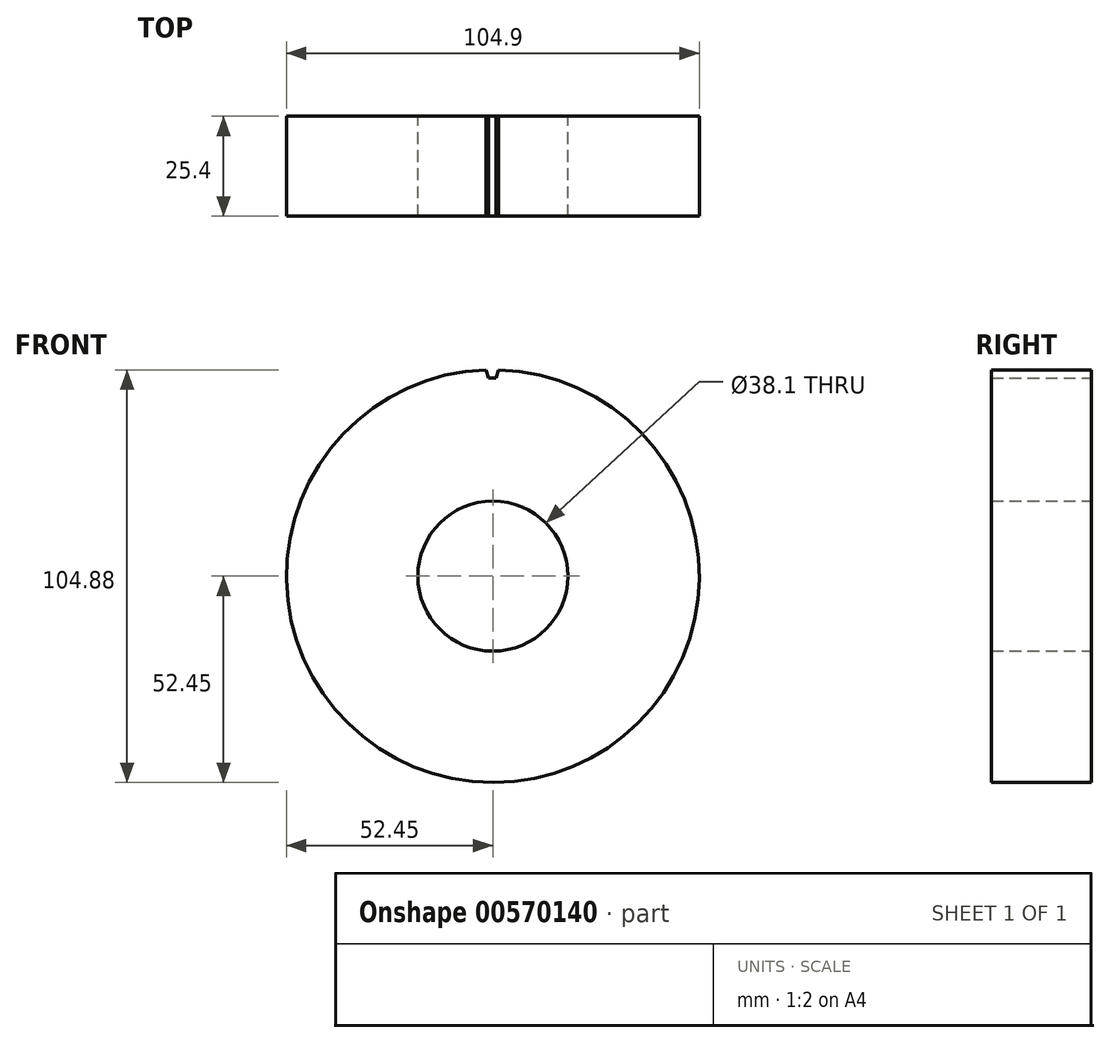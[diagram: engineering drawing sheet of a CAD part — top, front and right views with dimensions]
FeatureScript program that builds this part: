
annotation { "Feature Type Name" : "Feature", "Feature Type Description" : "" }
export const myFeature = defineFeature(function(context is Context, id is Id, definition is map)
    precondition{}
    {
        {
            var Q0;
            Q0=qCreatedBy(makeId("Front.planeOp"),FACE);
            var sketch = newSketch(context, id + "F0", { "sketchPlane" : qUnion([Q0])});
            skCircle(sketch, "E0", {"center": v(0, 0) * mm, "radius": 52.45 * mm});
            skCircle(sketch, "E1", {"center": v(0, 0) * mm, "radius": 19.05 * mm});
            skSolve(sketch);
        }
        {
            var Q0;
            Q0=makeQuery(id+"F0.imprint","IMPRINT",FACE,{"disambiguationData":[TD([[makeQuery(id+"F0.imprint","IMPRINT",EDGE,{"derivedFrom":sQuery(id+"F0.wireOp",EDGE,"E0")}),1.0]])]});
            extrude(context, id + "F1", {"entities" : qUnion([Q0]), "depth" : 25.4 * mm, "offsetDistance" : 25.4 * mm});
        }
        {
            var Q0;
            Q0=makeQuery(id+"F1.opExtrude","CAP_FACE",FACE,{"disambiguationData":[OSD([sQuery(id+"F0.wireOp",EDGE,"E0")])],"isStart":true});
            var sketch = newSketch(context, id + "F2", { "sketchPlane" : qUnion([Q0])});
            skLineSegment(sketch, "E2", {"start": v(-1.44, 52.43) * mm, "end": v(-0.83, 50.36) * mm});
            skLineSegment(sketch, "E3", {"start": v(-0.83, 50.36) * mm, "end": v(1.08, 50.36) * mm});
            skLineSegment(sketch, "E4", {"start": v(1.08, 50.36) * mm, "end": v(1.7, 52.42) * mm});
            skArc(sketch, "E5", {"start": v(1.7, 52.42) * mm, "mid": v(0.14, 52.45) * mm, "end": v(-1.44, 52.43) * mm});
            skSolve(sketch);
        }
        {
            var Q0;
            {var subQ0=sQuery(id+"F2.wireOp",EDGE,"E2");Q0=makeQuery(id+"F2.imprint","IMPRINT",FACE,{"disambiguationData":[TD([[makeQuery(id+"F2.imprint","IMPRINT",EDGE,{"derivedFrom":subQ0}),1.0]])]});}
            var Q1;
            Q1=makeQuery(id+"F32q0UH0prBzdGw_1.1.F2.imprint","IMPRINT",FACE,{"disambiguationData":[TD([[makeQuery(id+"F32q0UH0prBzdGw_1.1.F2.imprint","IMPRINT",EDGE,{"derivedFrom":sQuery(id+"F32q0UH0prBzdGw_1.1.F2.wireOp",EDGE,"E2")}),1.0]])]});
            var Q2;
            Q2=makeQuery(id+"F32q0UH0prBzdGw_1.2.F2.imprint","IMPRINT",FACE,{"disambiguationData":[TD([[makeQuery(id+"F32q0UH0prBzdGw_1.2.F2.imprint","IMPRINT",EDGE,{"derivedFrom":sQuery(id+"F32q0UH0prBzdGw_1.2.F2.wireOp",EDGE,"E2")}),1.0]])]});
            var Q3;
            Q3=makeQuery(id+"F32q0UH0prBzdGw_1.3.F2.imprint","IMPRINT",FACE,{"disambiguationData":[TD([[makeQuery(id+"F32q0UH0prBzdGw_1.3.F2.imprint","IMPRINT",EDGE,{"derivedFrom":sQuery(id+"F32q0UH0prBzdGw_1.3.F2.wireOp",EDGE,"E2")}),1.0]])]});
            var Q4;
            Q4=makeQuery(id+"F32q0UH0prBzdGw_1.4.F2.imprint","IMPRINT",FACE,{"disambiguationData":[TD([[makeQuery(id+"F32q0UH0prBzdGw_1.4.F2.imprint","IMPRINT",EDGE,{"derivedFrom":sQuery(id+"F32q0UH0prBzdGw_1.4.F2.wireOp",EDGE,"E2")}),1.0]])]});
            var Q5;
            Q5=makeQuery(id+"F32q0UH0prBzdGw_1.5.F2.imprint","IMPRINT",FACE,{"disambiguationData":[TD([[makeQuery(id+"F32q0UH0prBzdGw_1.5.F2.imprint","IMPRINT",EDGE,{"derivedFrom":sQuery(id+"F32q0UH0prBzdGw_1.5.F2.wireOp",EDGE,"E2")}),1.0]])]});
            var Q6;
            Q6=makeQuery(id+"F32q0UH0prBzdGw_1.59.F2.imprint","IMPRINT",FACE,{"disambiguationData":[TD([[makeQuery(id+"F32q0UH0prBzdGw_1.59.F2.imprint","IMPRINT",EDGE,{"derivedFrom":sQuery(id+"F32q0UH0prBzdGw_1.59.F2.wireOp",EDGE,"E2")}),1.0]])]});
            var Q7;
            Q7=makeQuery(id+"F32q0UH0prBzdGw_1.58.F2.imprint","IMPRINT",FACE,{"disambiguationData":[TD([[makeQuery(id+"F32q0UH0prBzdGw_1.58.F2.imprint","IMPRINT",EDGE,{"derivedFrom":sQuery(id+"F32q0UH0prBzdGw_1.58.F2.wireOp",EDGE,"E2")}),1.0]])]});
            var Q8;
            Q8=makeQuery(id+"F32q0UH0prBzdGw_1.6.F2.imprint","IMPRINT",FACE,{"disambiguationData":[TD([[makeQuery(id+"F32q0UH0prBzdGw_1.6.F2.imprint","IMPRINT",EDGE,{"derivedFrom":sQuery(id+"F32q0UH0prBzdGw_1.6.F2.wireOp",EDGE,"E2")}),1.0]])]});
            var Q9;
            Q9=makeQuery(id+"F32q0UH0prBzdGw_1.7.F2.imprint","IMPRINT",FACE,{"disambiguationData":[TD([[makeQuery(id+"F32q0UH0prBzdGw_1.7.F2.imprint","IMPRINT",EDGE,{"derivedFrom":sQuery(id+"F32q0UH0prBzdGw_1.7.F2.wireOp",EDGE,"E2")}),1.0]])]});
            var Q10;
            Q10=makeQuery(id+"F32q0UH0prBzdGw_1.8.F2.imprint","IMPRINT",FACE,{"disambiguationData":[TD([[makeQuery(id+"F32q0UH0prBzdGw_1.8.F2.imprint","IMPRINT",EDGE,{"derivedFrom":sQuery(id+"F32q0UH0prBzdGw_1.8.F2.wireOp",EDGE,"E2")}),1.0]])]});
            var Q11;
            Q11=makeQuery(id+"F32q0UH0prBzdGw_1.9.F2.imprint","IMPRINT",FACE,{"disambiguationData":[TD([[makeQuery(id+"F32q0UH0prBzdGw_1.9.F2.imprint","IMPRINT",EDGE,{"derivedFrom":sQuery(id+"F32q0UH0prBzdGw_1.9.F2.wireOp",EDGE,"E2")}),1.0]])]});
            var Q12;
            Q12=makeQuery(id+"F32q0UH0prBzdGw_1.10.F2.imprint","IMPRINT",FACE,{"disambiguationData":[TD([[makeQuery(id+"F32q0UH0prBzdGw_1.10.F2.imprint","IMPRINT",EDGE,{"derivedFrom":sQuery(id+"F32q0UH0prBzdGw_1.10.F2.wireOp",EDGE,"E2")}),1.0]])]});
            var Q13;
            Q13=makeQuery(id+"F32q0UH0prBzdGw_1.11.F2.imprint","IMPRINT",FACE,{"disambiguationData":[TD([[makeQuery(id+"F32q0UH0prBzdGw_1.11.F2.imprint","IMPRINT",EDGE,{"derivedFrom":sQuery(id+"F32q0UH0prBzdGw_1.11.F2.wireOp",EDGE,"E2")}),1.0]])]});
            var Q14;
            Q14=makeQuery(id+"F32q0UH0prBzdGw_1.12.F2.imprint","IMPRINT",FACE,{"disambiguationData":[TD([[makeQuery(id+"F32q0UH0prBzdGw_1.12.F2.imprint","IMPRINT",EDGE,{"derivedFrom":sQuery(id+"F32q0UH0prBzdGw_1.12.F2.wireOp",EDGE,"E2")}),1.0]])]});
            var Q15;
            Q15=makeQuery(id+"F32q0UH0prBzdGw_1.13.F2.imprint","IMPRINT",FACE,{"disambiguationData":[TD([[makeQuery(id+"F32q0UH0prBzdGw_1.13.F2.imprint","IMPRINT",EDGE,{"derivedFrom":sQuery(id+"F32q0UH0prBzdGw_1.13.F2.wireOp",EDGE,"E2")}),1.0]])]});
            var Q16;
            Q16=makeQuery(id+"F32q0UH0prBzdGw_1.14.F2.imprint","IMPRINT",FACE,{"disambiguationData":[TD([[makeQuery(id+"F32q0UH0prBzdGw_1.14.F2.imprint","IMPRINT",EDGE,{"derivedFrom":sQuery(id+"F32q0UH0prBzdGw_1.14.F2.wireOp",EDGE,"E2")}),1.0]])]});
            var Q17;
            Q17=makeQuery(id+"F32q0UH0prBzdGw_1.15.F2.imprint","IMPRINT",FACE,{"disambiguationData":[TD([[makeQuery(id+"F32q0UH0prBzdGw_1.15.F2.imprint","IMPRINT",EDGE,{"derivedFrom":sQuery(id+"F32q0UH0prBzdGw_1.15.F2.wireOp",EDGE,"E2")}),1.0]])]});
            var Q18;
            Q18=makeQuery(id+"F32q0UH0prBzdGw_1.17.F2.imprint","IMPRINT",FACE,{"disambiguationData":[TD([[makeQuery(id+"F32q0UH0prBzdGw_1.17.F2.imprint","IMPRINT",EDGE,{"derivedFrom":sQuery(id+"F32q0UH0prBzdGw_1.17.F2.wireOp",EDGE,"E2")}),1.0]])]});
            var Q19;
            Q19=makeQuery(id+"F32q0UH0prBzdGw_1.18.F2.imprint","IMPRINT",FACE,{"disambiguationData":[TD([[makeQuery(id+"F32q0UH0prBzdGw_1.18.F2.imprint","IMPRINT",EDGE,{"derivedFrom":sQuery(id+"F32q0UH0prBzdGw_1.18.F2.wireOp",EDGE,"E2")}),1.0]])]});
            var Q20;
            Q20=makeQuery(id+"F32q0UH0prBzdGw_1.19.F2.imprint","IMPRINT",FACE,{"disambiguationData":[TD([[makeQuery(id+"F32q0UH0prBzdGw_1.19.F2.imprint","IMPRINT",EDGE,{"derivedFrom":sQuery(id+"F32q0UH0prBzdGw_1.19.F2.wireOp",EDGE,"E2")}),1.0]])]});
            var Q21;
            Q21=makeQuery(id+"F32q0UH0prBzdGw_1.20.F2.imprint","IMPRINT",FACE,{"disambiguationData":[TD([[makeQuery(id+"F32q0UH0prBzdGw_1.20.F2.imprint","IMPRINT",EDGE,{"derivedFrom":sQuery(id+"F32q0UH0prBzdGw_1.20.F2.wireOp",EDGE,"E2")}),1.0]])]});
            var Q22;
            Q22=makeQuery(id+"F32q0UH0prBzdGw_1.21.F2.imprint","IMPRINT",FACE,{"disambiguationData":[TD([[makeQuery(id+"F32q0UH0prBzdGw_1.21.F2.imprint","IMPRINT",EDGE,{"derivedFrom":sQuery(id+"F32q0UH0prBzdGw_1.21.F2.wireOp",EDGE,"E2")}),1.0]])]});
            var Q23;
            Q23=makeQuery(id+"F32q0UH0prBzdGw_1.16.F2.imprint","IMPRINT",FACE,{"disambiguationData":[TD([[makeQuery(id+"F32q0UH0prBzdGw_1.16.F2.imprint","IMPRINT",EDGE,{"derivedFrom":sQuery(id+"F32q0UH0prBzdGw_1.16.F2.wireOp",EDGE,"E2")}),1.0]])]});
            var Q24;
            Q24=makeQuery(id+"F32q0UH0prBzdGw_1.22.F2.imprint","IMPRINT",FACE,{"disambiguationData":[TD([[makeQuery(id+"F32q0UH0prBzdGw_1.22.F2.imprint","IMPRINT",EDGE,{"derivedFrom":sQuery(id+"F32q0UH0prBzdGw_1.22.F2.wireOp",EDGE,"E2")}),1.0]])]});
            var Q25;
            Q25=makeQuery(id+"F32q0UH0prBzdGw_1.57.F2.imprint","IMPRINT",FACE,{"disambiguationData":[TD([[makeQuery(id+"F32q0UH0prBzdGw_1.57.F2.imprint","IMPRINT",EDGE,{"derivedFrom":sQuery(id+"F32q0UH0prBzdGw_1.57.F2.wireOp",EDGE,"E2")}),1.0]])]});
            var Q26;
            Q26=makeQuery(id+"F32q0UH0prBzdGw_1.56.F2.imprint","IMPRINT",FACE,{"disambiguationData":[TD([[makeQuery(id+"F32q0UH0prBzdGw_1.56.F2.imprint","IMPRINT",EDGE,{"derivedFrom":sQuery(id+"F32q0UH0prBzdGw_1.56.F2.wireOp",EDGE,"E2")}),1.0]])]});
            var Q27;
            Q27=makeQuery(id+"F32q0UH0prBzdGw_1.55.F2.imprint","IMPRINT",FACE,{"disambiguationData":[TD([[makeQuery(id+"F32q0UH0prBzdGw_1.55.F2.imprint","IMPRINT",EDGE,{"derivedFrom":sQuery(id+"F32q0UH0prBzdGw_1.55.F2.wireOp",EDGE,"E2")}),1.0]])]});
            var Q28;
            Q28=makeQuery(id+"F32q0UH0prBzdGw_1.54.F2.imprint","IMPRINT",FACE,{"disambiguationData":[TD([[makeQuery(id+"F32q0UH0prBzdGw_1.54.F2.imprint","IMPRINT",EDGE,{"derivedFrom":sQuery(id+"F32q0UH0prBzdGw_1.54.F2.wireOp",EDGE,"E2")}),1.0]])]});
            var Q29;
            Q29=makeQuery(id+"F32q0UH0prBzdGw_1.53.F2.imprint","IMPRINT",FACE,{"disambiguationData":[TD([[makeQuery(id+"F32q0UH0prBzdGw_1.53.F2.imprint","IMPRINT",EDGE,{"derivedFrom":sQuery(id+"F32q0UH0prBzdGw_1.53.F2.wireOp",EDGE,"E2")}),1.0]])]});
            var Q30;
            Q30=makeQuery(id+"F32q0UH0prBzdGw_1.52.F2.imprint","IMPRINT",FACE,{"disambiguationData":[TD([[makeQuery(id+"F32q0UH0prBzdGw_1.52.F2.imprint","IMPRINT",EDGE,{"derivedFrom":sQuery(id+"F32q0UH0prBzdGw_1.52.F2.wireOp",EDGE,"E2")}),1.0]])]});
            var Q31;
            Q31=makeQuery(id+"F32q0UH0prBzdGw_1.51.F2.imprint","IMPRINT",FACE,{"disambiguationData":[TD([[makeQuery(id+"F32q0UH0prBzdGw_1.51.F2.imprint","IMPRINT",EDGE,{"derivedFrom":sQuery(id+"F32q0UH0prBzdGw_1.51.F2.wireOp",EDGE,"E2")}),1.0]])]});
            var Q32;
            Q32=makeQuery(id+"F32q0UH0prBzdGw_1.50.F2.imprint","IMPRINT",FACE,{"disambiguationData":[TD([[makeQuery(id+"F32q0UH0prBzdGw_1.50.F2.imprint","IMPRINT",EDGE,{"derivedFrom":sQuery(id+"F32q0UH0prBzdGw_1.50.F2.wireOp",EDGE,"E2")}),1.0]])]});
            var Q33;
            Q33=makeQuery(id+"F32q0UH0prBzdGw_1.49.F2.imprint","IMPRINT",FACE,{"disambiguationData":[TD([[makeQuery(id+"F32q0UH0prBzdGw_1.49.F2.imprint","IMPRINT",EDGE,{"derivedFrom":sQuery(id+"F32q0UH0prBzdGw_1.49.F2.wireOp",EDGE,"E2")}),1.0]])]});
            var Q34;
            Q34=makeQuery(id+"F32q0UH0prBzdGw_1.48.F2.imprint","IMPRINT",FACE,{"disambiguationData":[TD([[makeQuery(id+"F32q0UH0prBzdGw_1.48.F2.imprint","IMPRINT",EDGE,{"derivedFrom":sQuery(id+"F32q0UH0prBzdGw_1.48.F2.wireOp",EDGE,"E2")}),1.0]])]});
            var Q35;
            Q35=makeQuery(id+"F32q0UH0prBzdGw_1.47.F2.imprint","IMPRINT",FACE,{"disambiguationData":[TD([[makeQuery(id+"F32q0UH0prBzdGw_1.47.F2.imprint","IMPRINT",EDGE,{"derivedFrom":sQuery(id+"F32q0UH0prBzdGw_1.47.F2.wireOp",EDGE,"E2")}),1.0]])]});
            var Q36;
            Q36=makeQuery(id+"F32q0UH0prBzdGw_1.46.F2.imprint","IMPRINT",FACE,{"disambiguationData":[TD([[makeQuery(id+"F32q0UH0prBzdGw_1.46.F2.imprint","IMPRINT",EDGE,{"derivedFrom":sQuery(id+"F32q0UH0prBzdGw_1.46.F2.wireOp",EDGE,"E2")}),1.0]])]});
            var Q37;
            Q37=makeQuery(id+"F32q0UH0prBzdGw_1.45.F2.imprint","IMPRINT",FACE,{"disambiguationData":[TD([[makeQuery(id+"F32q0UH0prBzdGw_1.45.F2.imprint","IMPRINT",EDGE,{"derivedFrom":sQuery(id+"F32q0UH0prBzdGw_1.45.F2.wireOp",EDGE,"E2")}),1.0]])]});
            var Q38;
            Q38=makeQuery(id+"F32q0UH0prBzdGw_1.44.F2.imprint","IMPRINT",FACE,{"disambiguationData":[TD([[makeQuery(id+"F32q0UH0prBzdGw_1.44.F2.imprint","IMPRINT",EDGE,{"derivedFrom":sQuery(id+"F32q0UH0prBzdGw_1.44.F2.wireOp",EDGE,"E2")}),1.0]])]});
            var Q39;
            Q39=makeQuery(id+"F32q0UH0prBzdGw_1.43.F2.imprint","IMPRINT",FACE,{"disambiguationData":[TD([[makeQuery(id+"F32q0UH0prBzdGw_1.43.F2.imprint","IMPRINT",EDGE,{"derivedFrom":sQuery(id+"F32q0UH0prBzdGw_1.43.F2.wireOp",EDGE,"E2")}),1.0]])]});
            var Q40;
            Q40=makeQuery(id+"F32q0UH0prBzdGw_1.42.F2.imprint","IMPRINT",FACE,{"disambiguationData":[TD([[makeQuery(id+"F32q0UH0prBzdGw_1.42.F2.imprint","IMPRINT",EDGE,{"derivedFrom":sQuery(id+"F32q0UH0prBzdGw_1.42.F2.wireOp",EDGE,"E2")}),1.0]])]});
            var Q41;
            Q41=makeQuery(id+"F32q0UH0prBzdGw_1.41.F2.imprint","IMPRINT",FACE,{"disambiguationData":[TD([[makeQuery(id+"F32q0UH0prBzdGw_1.41.F2.imprint","IMPRINT",EDGE,{"derivedFrom":sQuery(id+"F32q0UH0prBzdGw_1.41.F2.wireOp",EDGE,"E2")}),1.0]])]});
            var Q42;
            Q42=makeQuery(id+"F32q0UH0prBzdGw_1.40.F2.imprint","IMPRINT",FACE,{"disambiguationData":[TD([[makeQuery(id+"F32q0UH0prBzdGw_1.40.F2.imprint","IMPRINT",EDGE,{"derivedFrom":sQuery(id+"F32q0UH0prBzdGw_1.40.F2.wireOp",EDGE,"E2")}),1.0]])]});
            var Q43;
            Q43=makeQuery(id+"F32q0UH0prBzdGw_1.39.F2.imprint","IMPRINT",FACE,{"disambiguationData":[TD([[makeQuery(id+"F32q0UH0prBzdGw_1.39.F2.imprint","IMPRINT",EDGE,{"derivedFrom":sQuery(id+"F32q0UH0prBzdGw_1.39.F2.wireOp",EDGE,"E2")}),1.0]])]});
            var Q44;
            Q44=makeQuery(id+"F32q0UH0prBzdGw_1.38.F2.imprint","IMPRINT",FACE,{"disambiguationData":[TD([[makeQuery(id+"F32q0UH0prBzdGw_1.38.F2.imprint","IMPRINT",EDGE,{"derivedFrom":sQuery(id+"F32q0UH0prBzdGw_1.38.F2.wireOp",EDGE,"E2")}),1.0]])]});
            var Q45;
            Q45=makeQuery(id+"F32q0UH0prBzdGw_1.37.F2.imprint","IMPRINT",FACE,{"disambiguationData":[TD([[makeQuery(id+"F32q0UH0prBzdGw_1.37.F2.imprint","IMPRINT",EDGE,{"derivedFrom":sQuery(id+"F32q0UH0prBzdGw_1.37.F2.wireOp",EDGE,"E2")}),1.0]])]});
            var Q46;
            Q46=makeQuery(id+"F32q0UH0prBzdGw_1.36.F2.imprint","IMPRINT",FACE,{"disambiguationData":[TD([[makeQuery(id+"F32q0UH0prBzdGw_1.36.F2.imprint","IMPRINT",EDGE,{"derivedFrom":sQuery(id+"F32q0UH0prBzdGw_1.36.F2.wireOp",EDGE,"E2")}),1.0]])]});
            var Q47;
            Q47=makeQuery(id+"F32q0UH0prBzdGw_1.35.F2.imprint","IMPRINT",FACE,{"disambiguationData":[TD([[makeQuery(id+"F32q0UH0prBzdGw_1.35.F2.imprint","IMPRINT",EDGE,{"derivedFrom":sQuery(id+"F32q0UH0prBzdGw_1.35.F2.wireOp",EDGE,"E2")}),1.0]])]});
            var Q48;
            Q48=makeQuery(id+"F32q0UH0prBzdGw_1.34.F2.imprint","IMPRINT",FACE,{"disambiguationData":[TD([[makeQuery(id+"F32q0UH0prBzdGw_1.34.F2.imprint","IMPRINT",EDGE,{"derivedFrom":sQuery(id+"F32q0UH0prBzdGw_1.34.F2.wireOp",EDGE,"E2")}),1.0]])]});
            var Q49;
            Q49=makeQuery(id+"F32q0UH0prBzdGw_1.33.F2.imprint","IMPRINT",FACE,{"disambiguationData":[TD([[makeQuery(id+"F32q0UH0prBzdGw_1.33.F2.imprint","IMPRINT",EDGE,{"derivedFrom":sQuery(id+"F32q0UH0prBzdGw_1.33.F2.wireOp",EDGE,"E2")}),1.0]])]});
            var Q50;
            Q50=makeQuery(id+"F32q0UH0prBzdGw_1.32.F2.imprint","IMPRINT",FACE,{"disambiguationData":[TD([[makeQuery(id+"F32q0UH0prBzdGw_1.32.F2.imprint","IMPRINT",EDGE,{"derivedFrom":sQuery(id+"F32q0UH0prBzdGw_1.32.F2.wireOp",EDGE,"E2")}),1.0]])]});
            var Q51;
            Q51=makeQuery(id+"F32q0UH0prBzdGw_1.31.F2.imprint","IMPRINT",FACE,{"disambiguationData":[TD([[makeQuery(id+"F32q0UH0prBzdGw_1.31.F2.imprint","IMPRINT",EDGE,{"derivedFrom":sQuery(id+"F32q0UH0prBzdGw_1.31.F2.wireOp",EDGE,"E2")}),1.0]])]});
            var Q52;
            Q52=makeQuery(id+"F32q0UH0prBzdGw_1.30.F2.imprint","IMPRINT",FACE,{"disambiguationData":[TD([[makeQuery(id+"F32q0UH0prBzdGw_1.30.F2.imprint","IMPRINT",EDGE,{"derivedFrom":sQuery(id+"F32q0UH0prBzdGw_1.30.F2.wireOp",EDGE,"E2")}),1.0]])]});
            var Q53;
            Q53=makeQuery(id+"F32q0UH0prBzdGw_1.29.F2.imprint","IMPRINT",FACE,{"disambiguationData":[TD([[makeQuery(id+"F32q0UH0prBzdGw_1.29.F2.imprint","IMPRINT",EDGE,{"derivedFrom":sQuery(id+"F32q0UH0prBzdGw_1.29.F2.wireOp",EDGE,"E2")}),1.0]])]});
            var Q54;
            Q54=makeQuery(id+"F32q0UH0prBzdGw_1.28.F2.imprint","IMPRINT",FACE,{"disambiguationData":[TD([[makeQuery(id+"F32q0UH0prBzdGw_1.28.F2.imprint","IMPRINT",EDGE,{"derivedFrom":sQuery(id+"F32q0UH0prBzdGw_1.28.F2.wireOp",EDGE,"E2")}),1.0]])]});
            var Q55;
            Q55=makeQuery(id+"F32q0UH0prBzdGw_1.27.F2.imprint","IMPRINT",FACE,{"disambiguationData":[TD([[makeQuery(id+"F32q0UH0prBzdGw_1.27.F2.imprint","IMPRINT",EDGE,{"derivedFrom":sQuery(id+"F32q0UH0prBzdGw_1.27.F2.wireOp",EDGE,"E2")}),1.0]])]});
            var Q56;
            Q56=makeQuery(id+"F32q0UH0prBzdGw_1.26.F2.imprint","IMPRINT",FACE,{"disambiguationData":[TD([[makeQuery(id+"F32q0UH0prBzdGw_1.26.F2.imprint","IMPRINT",EDGE,{"derivedFrom":sQuery(id+"F32q0UH0prBzdGw_1.26.F2.wireOp",EDGE,"E2")}),1.0]])]});
            var Q57;
            Q57=makeQuery(id+"F32q0UH0prBzdGw_1.25.F2.imprint","IMPRINT",FACE,{"disambiguationData":[TD([[makeQuery(id+"F32q0UH0prBzdGw_1.25.F2.imprint","IMPRINT",EDGE,{"derivedFrom":sQuery(id+"F32q0UH0prBzdGw_1.25.F2.wireOp",EDGE,"E2")}),1.0]])]});
            var Q58;
            Q58=makeQuery(id+"F32q0UH0prBzdGw_1.24.F2.imprint","IMPRINT",FACE,{"disambiguationData":[TD([[makeQuery(id+"F32q0UH0prBzdGw_1.24.F2.imprint","IMPRINT",EDGE,{"derivedFrom":sQuery(id+"F32q0UH0prBzdGw_1.24.F2.wireOp",EDGE,"E2")}),1.0]])]});
            var Q59;
            Q59=makeQuery(id+"F32q0UH0prBzdGw_1.23.F2.imprint","IMPRINT",FACE,{"disambiguationData":[TD([[makeQuery(id+"F32q0UH0prBzdGw_1.23.F2.imprint","IMPRINT",EDGE,{"derivedFrom":sQuery(id+"F32q0UH0prBzdGw_1.23.F2.wireOp",EDGE,"E2")}),1.0]])]});
            extrude(context, id + "F3", {"entities" : qUnion([Q0, Q1, Q2, Q3, Q4, Q5, Q6, Q7, Q8, Q9, Q10, Q11, Q12, Q13, Q14, Q15, Q16, Q17, Q18, Q19, Q20, Q21, Q22, Q23, Q24, Q25, Q26, Q27, Q28, Q29, Q30, Q31, Q32, Q33, Q34, Q35, Q36, Q37, Q38, Q39, Q40, Q41, Q42, Q43, Q44, Q45, Q46, Q47, Q48, Q49, Q50, Q51, Q52, Q53, Q54, Q55, Q56, Q57, Q58, Q59]), "operationType" : NewBodyOperationType.REMOVE, "oppositeDirection" : true, "depth" : 25.4 * mm, "offsetDistance" : 25.4 * mm});
        }
    });
